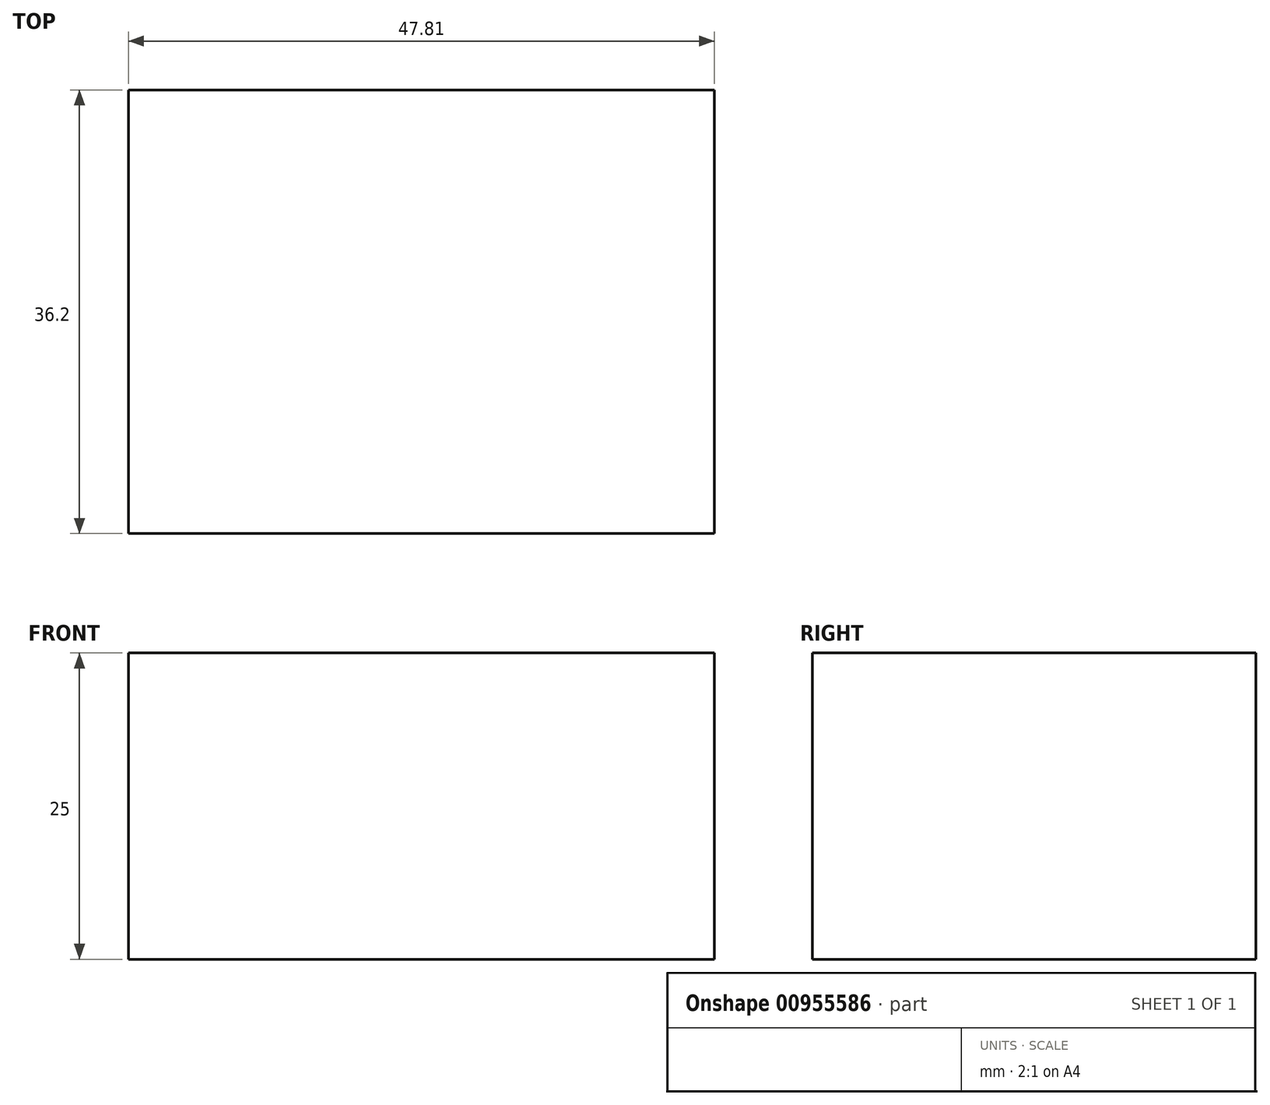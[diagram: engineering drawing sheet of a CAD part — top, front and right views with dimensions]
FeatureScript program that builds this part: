
annotation { "Feature Type Name" : "Feature", "Feature Type Description" : "" }
export const myFeature = defineFeature(function(context is Context, id is Id, definition is map)
    precondition{}
    {
        {
            var Q0;
            Q0=qCreatedBy(makeId("Top.planeOp"),FACE);
            var sketch = newSketch(context, id + "F0", { "sketchPlane" : qUnion([Q0])});
            skLineSegment(sketch, "E0.bottom", {"start": v(-61.83, 34.13) * mm, "end": v(-14.02, 34.13) * mm});
            skLineSegment(sketch, "E0.top", {"start": v(-61.83, -2.07) * mm, "end": v(-14.02, -2.07) * mm});
            skLineSegment(sketch, "E0.left", {"start": v(-61.83, 34.13) * mm, "end": v(-61.83, -2.07) * mm});
            skLineSegment(sketch, "E0.right", {"start": v(-14.02, 34.13) * mm, "end": v(-14.02, -2.07) * mm});
            skSolve(sketch);
        }
        {
            var Q0;
            Q0=makeQuery(id+"F0.imprint","IMPRINT",FACE,{"disambiguationData":[TD([[makeQuery(id+"F0.imprint","IMPRINT",EDGE,{"derivedFrom":sQuery(id+"F0.wireOp",EDGE,"E0.bottom")}),-1.0]])]});
            extrude(context, id + "F1", {"entities" : qUnion([Q0]), "depth" : 25 * mm, "offsetDistance" : 25 * mm});
        }
    });
